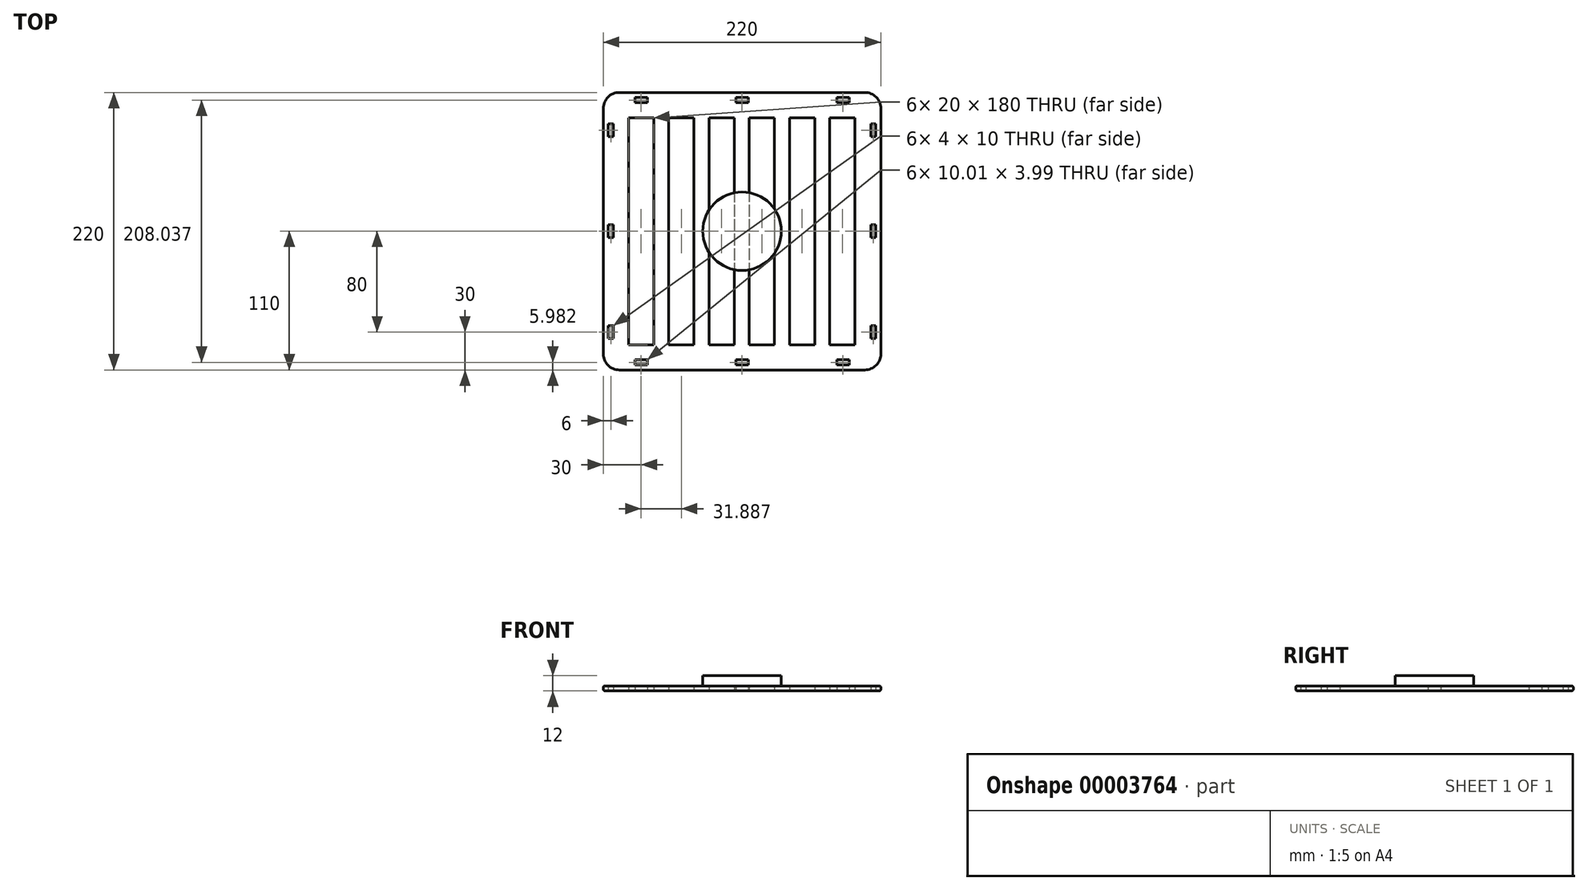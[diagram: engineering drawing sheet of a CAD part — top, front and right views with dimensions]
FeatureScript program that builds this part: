
annotation { "Feature Type Name" : "Feature", "Feature Type Description" : "" }
export const myFeature = defineFeature(function(context is Context, id is Id, definition is map)
    precondition{}
    {
        {
            var Q0;
            Q0=qCreatedBy(makeId("Top.planeOp"),FACE);
            var sketch = newSketch(context, id + "F0", { "sketchPlane" : qUnion([Q0])});
            skLineSegment(sketch, "E0.bottom", {"start": v(-97.3, 110) * mm, "end": v(97.3, 110) * mm});
            skLineSegment(sketch, "E0.top", {"start": v(-97.3, -110) * mm, "end": v(97.3, -110) * mm});
            skLineSegment(sketch, "E0.left", {"start": v(-110, 97.3) * mm, "end": v(-110, -97.3) * mm});
            skLineSegment(sketch, "E0.right", {"start": v(110, 97.3) * mm, "end": v(110, -97.3) * mm});
            skLineSegment(sketch, "E1.bottom", {"start": v(-90, 90) * mm, "end": v(-70, 90) * mm});
            skLineSegment(sketch, "E1.top", {"start": v(-90, -90) * mm, "end": v(-70, -90) * mm});
            skLineSegment(sketch, "E1.left", {"start": v(-90, 90) * mm, "end": v(-90, -90) * mm});
            skLineSegment(sketch, "E1.right", {"start": v(-70, 90) * mm, "end": v(-70, -90) * mm});
            skLineSegment(sketch, "E2.1.0.0", {"start": v(-58.11, 90) * mm, "end": v(-38.11, 90) * mm});
            skLineSegment(sketch, "E2.1.0.1", {"start": v(-38.11, 90) * mm, "end": v(-38.11, -90) * mm});
            skLineSegment(sketch, "E2.1.0.2", {"start": v(-58.11, 90) * mm, "end": v(-58.11, -90) * mm});
            skLineSegment(sketch, "E2.1.0.3", {"start": v(-58.11, -90) * mm, "end": v(-38.11, -90) * mm});
            skLineSegment(sketch, "E2.2.0.0", {"start": v(-26.23, 90) * mm, "end": v(-6.23, 90) * mm});
            skLineSegment(sketch, "E2.2.0.1", {"start": v(-6.23, 90) * mm, "end": v(-6.23, -90) * mm});
            skLineSegment(sketch, "E2.2.0.2", {"start": v(-26.23, 90) * mm, "end": v(-26.23, -90) * mm});
            skLineSegment(sketch, "E2.2.0.3", {"start": v(-26.23, -90) * mm, "end": v(-6.23, -90) * mm});
            skLineSegment(sketch, "E2.3.0.0", {"start": v(5.66, 90) * mm, "end": v(25.66, 90) * mm});
            skLineSegment(sketch, "E2.3.0.1", {"start": v(25.66, 90) * mm, "end": v(25.66, -90) * mm});
            skLineSegment(sketch, "E2.3.0.2", {"start": v(5.66, 90) * mm, "end": v(5.66, -90) * mm});
            skLineSegment(sketch, "E2.3.0.3", {"start": v(5.66, -90) * mm, "end": v(25.66, -90) * mm});
            skLineSegment(sketch, "E2.4.0.0", {"start": v(37.55, 90) * mm, "end": v(57.55, 90) * mm});
            skLineSegment(sketch, "E2.4.0.1", {"start": v(57.55, 90) * mm, "end": v(57.55, -90) * mm});
            skLineSegment(sketch, "E2.4.0.2", {"start": v(37.55, 90) * mm, "end": v(37.55, -90) * mm});
            skLineSegment(sketch, "E2.4.0.3", {"start": v(37.55, -90) * mm, "end": v(57.55, -90) * mm});
            skLineSegment(sketch, "E2.5.0.0", {"start": v(69.44, 90) * mm, "end": v(89.44, 90) * mm});
            skLineSegment(sketch, "E2.5.0.1", {"start": v(89.44, 90) * mm, "end": v(89.44, -90) * mm});
            skLineSegment(sketch, "E2.5.0.2", {"start": v(69.44, 90) * mm, "end": v(69.44, -90) * mm});
            skLineSegment(sketch, "E2.5.0.3", {"start": v(69.44, -90) * mm, "end": v(89.44, -90) * mm});
            skLineSegment(sketch, "E2.direction1", {"start": v(-90, 90) * mm, "end": v(-58.11, 90) * mm, "construction": true});
            skLineSegment(sketch, "E3", {"start": v(0, 0) * mm, "end": v(-110, 0) * mm, "construction": true});
            skLineSegment(sketch, "E4", {"start": v(0, 0) * mm, "end": v(110, 0) * mm, "construction": true});
            skLineSegment(sketch, "E5.rect.bottom", {"start": v(-106, 5) * mm, "end": v(-102, 5) * mm});
            skLineSegment(sketch, "E5.rect.top", {"start": v(-106, -5) * mm, "end": v(-102, -5) * mm});
            skLineSegment(sketch, "E5.rect.left", {"start": v(-106, 5) * mm, "end": v(-106, -5) * mm});
            skLineSegment(sketch, "E5.rect.right", {"start": v(-102, 5) * mm, "end": v(-102, -5) * mm});
            skPoint(sketch, "E5.rect.middle", {"position": v(-104, 0) * mm});
            skLineSegment(sketch, "E6", {"start": v(0, 0) * mm, "end": v(0, 110) * mm, "construction": true});
            skLineSegment(sketch, "E7.0.MirrorCS", {"start": v(106, -5) * mm, "end": v(102, -5) * mm});
            skLineSegment(sketch, "E8.0.MirrorCS", {"start": v(102, 5) * mm, "end": v(102, -5) * mm});
            skLineSegment(sketch, "E9.0.MirrorCS", {"start": v(106, 5) * mm, "end": v(102, 5) * mm});
            skLineSegment(sketch, "E10.0.MirrorCS", {"start": v(106, 5) * mm, "end": v(106, -5) * mm});
            skLineSegment(sketch, "E11.0.1.0", {"start": v(-106, 85) * mm, "end": v(-102, 85) * mm});
            skPoint(sketch, "E11.0.1.1", {"position": v(-104, 80) * mm});
            skLineSegment(sketch, "E11.0.1.2", {"start": v(-102, 85) * mm, "end": v(-102, 75) * mm});
            skLineSegment(sketch, "E11.0.1.3", {"start": v(-106, 75) * mm, "end": v(-102, 75) * mm});
            skLineSegment(sketch, "E11.0.1.4", {"start": v(-106, 85) * mm, "end": v(-106, 75) * mm});
            skLineSegment(sketch, "E11.0.1.5", {"start": v(-58.11, 170) * mm, "end": v(-58.11, -10) * mm});
            skLineSegment(sketch, "E11.direction1", {"start": v(-106, 5) * mm, "end": v(-80.6, 5) * mm, "construction": true});
            skLineSegment(sketch, "E11.direction2", {"start": v(-106, 5) * mm, "end": v(-106, 85) * mm, "construction": true});
            skLineSegment(sketch, "E12.0.1.0", {"start": v(-106, -75) * mm, "end": v(-102, -75) * mm});
            skLineSegment(sketch, "E12.0.1.1", {"start": v(-102, -75) * mm, "end": v(-102, -85) * mm});
            skLineSegment(sketch, "E12.0.1.2", {"start": v(-106, -75) * mm, "end": v(-106, -85) * mm});
            skLineSegment(sketch, "E12.0.1.3", {"start": v(-106, -85) * mm, "end": v(-102, -85) * mm});
            skLineSegment(sketch, "E12.direction2", {"start": v(-106, 5) * mm, "end": v(-106, -75) * mm, "construction": true});
            skLineSegment(sketch, "E13.0.MirrorCS", {"start": v(106, 85) * mm, "end": v(102, 85) * mm});
            skLineSegment(sketch, "E14.0.MirrorCS", {"start": v(106, 85) * mm, "end": v(106, 75) * mm});
            skLineSegment(sketch, "E15.0.MirrorCS", {"start": v(106, 75) * mm, "end": v(102, 75) * mm});
            skLineSegment(sketch, "E16.0.MirrorCS", {"start": v(102, 85) * mm, "end": v(102, 75) * mm});
            skLineSegment(sketch, "E17.0.MirrorCS", {"start": v(106, -75) * mm, "end": v(102, -75) * mm});
            skLineSegment(sketch, "E18.0.MirrorCS", {"start": v(106, -75) * mm, "end": v(106, -85) * mm});
            skLineSegment(sketch, "E19.0.MirrorCS", {"start": v(106, -85) * mm, "end": v(102, -85) * mm});
            skLineSegment(sketch, "E20.0.MirrorCS", {"start": v(102, -75) * mm, "end": v(102, -85) * mm});
            skLineSegment(sketch, "E21.rect.bottom", {"start": v(-5, 102.02) * mm, "end": v(5, 102.02) * mm});
            skLineSegment(sketch, "E21.rect.top", {"start": v(-5, 106.01) * mm, "end": v(5, 106.01) * mm});
            skLineSegment(sketch, "E21.rect.left", {"start": v(-5, 102.02) * mm, "end": v(-5, 106.01) * mm});
            skLineSegment(sketch, "E21.rect.right", {"start": v(5, 102.02) * mm, "end": v(5, 106.01) * mm});
            skPoint(sketch, "E21.rect.middle", {"position": v(0, 104.02) * mm});
            skLineSegment(sketch, "E22.1.0.0", {"start": v(75, 106.01) * mm, "end": v(85, 106.01) * mm});
            skLineSegment(sketch, "E22.1.0.1", {"start": v(75, 102.02) * mm, "end": v(75, 106.01) * mm});
            skLineSegment(sketch, "E22.1.0.2", {"start": v(75, 102.02) * mm, "end": v(85, 102.02) * mm});
            skLineSegment(sketch, "E22.1.0.3", {"start": v(85, 102.02) * mm, "end": v(85, 106.01) * mm});
            skLineSegment(sketch, "E22.direction1", {"start": v(-5, 106.01) * mm, "end": v(75, 106.01) * mm, "construction": true});
            skLineSegment(sketch, "E23.1.0.0", {"start": v(-85, 106.01) * mm, "end": v(-75, 106.01) * mm});
            skLineSegment(sketch, "E23.1.0.1", {"start": v(-85, 102.02) * mm, "end": v(-85, 106.01) * mm});
            skLineSegment(sketch, "E23.1.0.2", {"start": v(-85, 102.02) * mm, "end": v(-75, 102.02) * mm});
            skLineSegment(sketch, "E23.1.0.3", {"start": v(-75, 102.02) * mm, "end": v(-75, 106.01) * mm});
            skLineSegment(sketch, "E23.direction1", {"start": v(-5, 106.01) * mm, "end": v(-85, 106.01) * mm, "construction": true});
            skLineSegment(sketch, "E24.0.MirrorCS", {"start": v(-85, -106.01) * mm, "end": v(-75, -106.01) * mm});
            skLineSegment(sketch, "E25.0.MirrorCS", {"start": v(-85, -102.02) * mm, "end": v(-75, -102.02) * mm});
            skLineSegment(sketch, "E26.0.MirrorCS", {"start": v(-75, -102.02) * mm, "end": v(-75, -106.01) * mm});
            skLineSegment(sketch, "E27.0.MirrorCS", {"start": v(-85, -102.02) * mm, "end": v(-85, -106.01) * mm});
            skLineSegment(sketch, "E28.0.MirrorCS", {"start": v(-5, -106.01) * mm, "end": v(5, -106.01) * mm});
            skLineSegment(sketch, "E29.0.MirrorCS", {"start": v(-5, -102.02) * mm, "end": v(-5, -106.01) * mm});
            skLineSegment(sketch, "E30.0.MirrorCS", {"start": v(-5, -102.02) * mm, "end": v(5, -102.02) * mm});
            skLineSegment(sketch, "E31.0.MirrorCS", {"start": v(5, -102.02) * mm, "end": v(5, -106.01) * mm});
            skLineSegment(sketch, "E32.0.MirrorCS", {"start": v(75, -106.01) * mm, "end": v(85, -106.01) * mm});
            skLineSegment(sketch, "E33.0.MirrorCS", {"start": v(85, -102.02) * mm, "end": v(85, -106.01) * mm});
            skLineSegment(sketch, "E34.0.MirrorCS", {"start": v(75, -102.02) * mm, "end": v(85, -102.02) * mm});
            skLineSegment(sketch, "E35.0.MirrorCS", {"start": v(75, -102.02) * mm, "end": v(75, -106.01) * mm});
            skPoint(sketch, "E36.visualSharp", {"position": v(-110, 110) * mm});
            skArc(sketch, "E36.filletArc", {"start": v(-97.3, 110) * mm, "mid": v(-106.28, 106.28) * mm, "end": v(-110, 97.3) * mm});
            skPoint(sketch, "E37.visualSharp", {"position": v(-110, -110) * mm});
            skArc(sketch, "E37.filletArc", {"start": v(-110, -97.3) * mm, "mid": v(-106.28, -106.28) * mm, "end": v(-97.3, -110) * mm});
            skPoint(sketch, "E38.visualSharp", {"position": v(110, -110) * mm});
            skArc(sketch, "E38.filletArc", {"start": v(97.3, -110) * mm, "mid": v(106.28, -106.28) * mm, "end": v(110, -97.3) * mm});
            skPoint(sketch, "E39.visualSharp", {"position": v(110, 110) * mm});
            skArc(sketch, "E39.filletArc", {"start": v(110, 97.3) * mm, "mid": v(106.28, 106.28) * mm, "end": v(97.3, 110) * mm});
            skSolve(sketch);
        }
        {
            var Q0;
            Q0=makeQuery(id+"F0.imprint","IMPRINT",FACE,{"disambiguationData":[TD([[makeQuery(id+"F0.imprint","IMPRINT",EDGE,{"derivedFrom":sQuery(id+"F0.wireOp",EDGE,"E0.top")}),1.0]])]});
            extrude(context, id + "F1", {"entities" : qUnion([Q0]), "depth" : 4 * mm});
        }
        {
            var Q0;
            Q0=makeQuery(id+"F1.opExtrude","CAP_FACE",FACE,{"disambiguationData":[OSD([sQuery(id+"F0.wireOp",EDGE,"E0.bottom"),sQuery(id+"F0.wireOp",EDGE,"E0.top"),sQuery(id+"F0.wireOp",EDGE,"E0.left"),sQuery(id+"F0.wireOp",EDGE,"E0.right"),sQuery(id+"F0.wireOp",EDGE,"E1.bottom"),sQuery(id+"F0.wireOp",EDGE,"E1.top"),sQuery(id+"F0.wireOp",EDGE,"E1.left"),sQuery(id+"F0.wireOp",EDGE,"E1.right"),sQuery(id+"F0.wireOp",EDGE,"E2.1.0.0"),sQuery(id+"F0.wireOp",EDGE,"E2.1.0.1"),sQuery(id+"F0.wireOp",EDGE,"E2.1.0.2"),sQuery(id+"F0.wireOp",EDGE,"E2.1.0.3"),sQuery(id+"F0.wireOp",EDGE,"E2.2.0.0"),sQuery(id+"F0.wireOp",EDGE,"E2.2.0.1"),sQuery(id+"F0.wireOp",EDGE,"E2.2.0.2"),sQuery(id+"F0.wireOp",EDGE,"E2.2.0.3"),sQuery(id+"F0.wireOp",EDGE,"E2.3.0.0"),sQuery(id+"F0.wireOp",EDGE,"E2.3.0.1"),sQuery(id+"F0.wireOp",EDGE,"E2.3.0.2"),sQuery(id+"F0.wireOp",EDGE,"E2.3.0.3"),sQuery(id+"F0.wireOp",EDGE,"E2.4.0.0"),sQuery(id+"F0.wireOp",EDGE,"E2.4.0.1"),sQuery(id+"F0.wireOp",EDGE,"E2.4.0.2"),sQuery(id+"F0.wireOp",EDGE,"E2.4.0.3"),sQuery(id+"F0.wireOp",EDGE,"E2.5.0.0"),sQuery(id+"F0.wireOp",EDGE,"E2.5.0.1"),sQuery(id+"F0.wireOp",EDGE,"E2.5.0.2"),sQuery(id+"F0.wireOp",EDGE,"E2.5.0.3"),sQuery(id+"F0.wireOp",EDGE,"E5.rect.bottom"),sQuery(id+"F0.wireOp",EDGE,"E5.rect.top"),sQuery(id+"F0.wireOp",EDGE,"E5.rect.left"),sQuery(id+"F0.wireOp",EDGE,"E5.rect.right"),sQuery(id+"F0.wireOp",EDGE,"E7.0.MirrorCS"),sQuery(id+"F0.wireOp",EDGE,"E8.0.MirrorCS"),sQuery(id+"F0.wireOp",EDGE,"E9.0.MirrorCS"),sQuery(id+"F0.wireOp",EDGE,"E10.0.MirrorCS"),sQuery(id+"F0.wireOp",EDGE,"E11.0.1.0"),sQuery(id+"F0.wireOp",EDGE,"E11.0.1.2"),sQuery(id+"F0.wireOp",EDGE,"E11.0.1.3"),sQuery(id+"F0.wireOp",EDGE,"E11.0.1.4"),sQuery(id+"F0.wireOp",EDGE,"E11.0.1.5"),sQuery(id+"F0.wireOp",EDGE,"E12.0.1.0"),sQuery(id+"F0.wireOp",EDGE,"E12.0.1.1"),sQuery(id+"F0.wireOp",EDGE,"E12.0.1.2"),sQuery(id+"F0.wireOp",EDGE,"E12.0.1.3"),sQuery(id+"F0.wireOp",EDGE,"E13.0.MirrorCS"),sQuery(id+"F0.wireOp",EDGE,"E14.0.MirrorCS"),sQuery(id+"F0.wireOp",EDGE,"E15.0.MirrorCS"),sQuery(id+"F0.wireOp",EDGE,"E16.0.MirrorCS"),sQuery(id+"F0.wireOp",EDGE,"E17.0.MirrorCS"),sQuery(id+"F0.wireOp",EDGE,"E18.0.MirrorCS"),sQuery(id+"F0.wireOp",EDGE,"E19.0.MirrorCS"),sQuery(id+"F0.wireOp",EDGE,"E20.0.MirrorCS"),sQuery(id+"F0.wireOp",EDGE,"E21.rect.bottom"),sQuery(id+"F0.wireOp",EDGE,"E21.rect.top"),sQuery(id+"F0.wireOp",EDGE,"E21.rect.left"),sQuery(id+"F0.wireOp",EDGE,"E21.rect.right"),sQuery(id+"F0.wireOp",EDGE,"E22.1.0.0"),sQuery(id+"F0.wireOp",EDGE,"E22.1.0.1"),sQuery(id+"F0.wireOp",EDGE,"E22.1.0.2"),sQuery(id+"F0.wireOp",EDGE,"E22.1.0.3"),sQuery(id+"F0.wireOp",EDGE,"E23.1.0.0"),sQuery(id+"F0.wireOp",EDGE,"E23.1.0.1"),sQuery(id+"F0.wireOp",EDGE,"E23.1.0.2"),sQuery(id+"F0.wireOp",EDGE,"E23.1.0.3"),sQuery(id+"F0.wireOp",EDGE,"E24.0.MirrorCS"),sQuery(id+"F0.wireOp",EDGE,"E25.0.MirrorCS"),sQuery(id+"F0.wireOp",EDGE,"E26.0.MirrorCS"),sQuery(id+"F0.wireOp",EDGE,"E27.0.MirrorCS"),sQuery(id+"F0.wireOp",EDGE,"E28.0.MirrorCS"),sQuery(id+"F0.wireOp",EDGE,"E29.0.MirrorCS"),sQuery(id+"F0.wireOp",EDGE,"E30.0.MirrorCS"),sQuery(id+"F0.wireOp",EDGE,"E31.0.MirrorCS"),sQuery(id+"F0.wireOp",EDGE,"E32.0.MirrorCS"),sQuery(id+"F0.wireOp",EDGE,"E33.0.MirrorCS"),sQuery(id+"F0.wireOp",EDGE,"E34.0.MirrorCS"),sQuery(id+"F0.wireOp",EDGE,"E35.0.MirrorCS"),sQuery(id+"F0.wireOp",EDGE,"E36.filletArc"),sQuery(id+"F0.wireOp",EDGE,"E37.filletArc"),sQuery(id+"F0.wireOp",EDGE,"E38.filletArc"),sQuery(id+"F0.wireOp",EDGE,"E39.filletArc")])],"isStart":false});
            var sketch = newSketch(context, id + "F2", { "sketchPlane" : qUnion([Q0])});
            skCircle(sketch, "E40", {"center": v(0, 0) * mm, "radius": 31.11 * mm});
            skSolve(sketch);
        }
        {
            var Q0;
            {var subQ0=makeQuery(id+"F1.opExtrude","CAP_EDGE",EDGE,{"disambiguationData":[OSD([sQuery(id+"F0.wireOp",EDGE,"E2.3.0.2")])],"isStart":false});var subQ1=sQuery(id+"F2.wireOp",EDGE,"E40");var subQ3=makeQuery(id+"F2.imprint","INTERSECT",VERTEX,{"disambiguationData":[OD(0.0)],"derivedFrom":[subQ0,subQ1]});Q0=makeQuery(id+"F2.imprint","IMPRINT",FACE,{"disambiguationData":[TD([[makeQuery(id+"F2.imprint","IMPRINT",EDGE,{"disambiguationData":[TD([[subQ3,1.0]])],"derivedFrom":subQ1}),1.0]])]});}
            var Q1;
            {var subQ0=makeQuery(id+"F1.opExtrude","CAP_EDGE",EDGE,{"disambiguationData":[OSD([sQuery(id+"F0.wireOp",EDGE,"E2.3.0.1")])],"isStart":false});var subQ1=sQuery(id+"F2.wireOp",EDGE,"E40");var subQ3=makeQuery(id+"F2.imprint","INTERSECT",VERTEX,{"disambiguationData":[OD(0.0)],"derivedFrom":[subQ0,subQ1]});Q1=makeQuery(id+"F2.imprint","IMPRINT",FACE,{"disambiguationData":[TD([[makeQuery(id+"F2.imprint","IMPRINT",EDGE,{"disambiguationData":[TD([[subQ3,1.0]])],"derivedFrom":subQ1}),1.0]])]});}
            var Q2;
            {var subQ0=makeQuery(id+"F1.opExtrude","CAP_EDGE",EDGE,{"disambiguationData":[OSD([sQuery(id+"F0.wireOp",EDGE,"E2.3.0.2")])],"isStart":false});var subQ1=sQuery(id+"F2.wireOp",EDGE,"E40");var subQ3=makeQuery(id+"F2.imprint","INTERSECT",VERTEX,{"disambiguationData":[OD(0.0)],"derivedFrom":[subQ0,subQ1]});Q2=makeQuery(id+"F2.imprint","IMPRINT",FACE,{"disambiguationData":[TD([[makeQuery(id+"F2.imprint","IMPRINT",EDGE,{"disambiguationData":[TD([[subQ3,-1.0]])],"derivedFrom":subQ1}),1.0]])]});}
            var Q3;
            {var subQ0=makeQuery(id+"F1.opExtrude","CAP_EDGE",EDGE,{"disambiguationData":[OSD([sQuery(id+"F0.wireOp",EDGE,"E2.2.0.1")])],"isStart":false});var subQ1=sQuery(id+"F2.wireOp",EDGE,"E40");var subQ3=makeQuery(id+"F2.imprint","INTERSECT",VERTEX,{"disambiguationData":[OD(0.0)],"derivedFrom":[subQ0,subQ1]});Q3=makeQuery(id+"F2.imprint","IMPRINT",FACE,{"disambiguationData":[TD([[makeQuery(id+"F2.imprint","IMPRINT",EDGE,{"disambiguationData":[TD([[subQ3,-1.0]])],"derivedFrom":subQ1}),1.0]])]});}
            var Q4;
            {var subQ0=makeQuery(id+"F1.opExtrude","CAP_EDGE",EDGE,{"disambiguationData":[OSD([sQuery(id+"F0.wireOp",EDGE,"E2.2.0.2")])],"isStart":false});var subQ1=sQuery(id+"F2.wireOp",EDGE,"E40");var subQ3=makeQuery(id+"F2.imprint","INTERSECT",VERTEX,{"disambiguationData":[OD(0.0)],"derivedFrom":[subQ0,subQ1]});Q4=makeQuery(id+"F2.imprint","IMPRINT",FACE,{"disambiguationData":[TD([[makeQuery(id+"F2.imprint","IMPRINT",EDGE,{"disambiguationData":[TD([[subQ3,-1.0]])],"derivedFrom":subQ1}),1.0]])]});}
            extrude(context, id + "F3", {"entities" : qUnion([Q0, Q1, Q2, Q3, Q4]), "depth" : 8 * mm});
        }
        {
            var Q0;
            Q0=makeQuery(id+"F1.opExtrude","CAP_EDGE",EDGE,{"disambiguationData":[OSD([sQuery(id+"F0.wireOp",EDGE,"E0.top")])],"isStart":false});
            var Q1;
            Q1=makeQuery(id+"F1.opExtrude","CAP_EDGE",EDGE,{"disambiguationData":[OSD([sQuery(id+"F0.wireOp",EDGE,"E0.left")])],"isStart":false});
            var Q2;
            Q2=makeQuery(id+"F1.opExtrude","CAP_EDGE",EDGE,{"disambiguationData":[OSD([sQuery(id+"F0.wireOp",EDGE,"E0.bottom")])],"isStart":false});
            var Q3;
            Q3=makeQuery(id+"F1.opExtrude","CAP_EDGE",EDGE,{"disambiguationData":[OSD([sQuery(id+"F0.wireOp",EDGE,"E0.right")])],"isStart":false});
            var Q4;
            Q4=makeQuery(id+"F1.opExtrude","CAP_EDGE",EDGE,{"disambiguationData":[OSD([sQuery(id+"F0.wireOp",EDGE,"E0.right")])],"isStart":true});
            var Q5;
            Q5=makeQuery(id+"F1.opExtrude","CAP_EDGE",EDGE,{"disambiguationData":[OSD([sQuery(id+"F0.wireOp",EDGE,"E0.bottom")])],"isStart":true});
            var Q6;
            {var subQ0=sQuery(id+"F0.wireOp",EDGE,"E0.bottom");var subQ1=sQuery(id+"F0.wireOp",EDGE,"E39.filletArc");var subQ2=sQuery(id+"F0.wireOp",EDGE,"E0.right");Q6=qUnion([makeQuery(id+"F1.opExtrude","SWEPT_EDGE",EDGE,{"disambiguationData":[OSD([subQ0,sQuery(id+"F0.wireOp",EDGE,"E36.filletArc")])]}),makeQuery(id+"F1.opExtrude","SWEPT_EDGE",EDGE,{"disambiguationData":[OSD([subQ0,subQ1])]}),makeQuery(id+"F1.opExtrude","SWEPT_EDGE",EDGE,{"disambiguationData":[OSD([subQ2,subQ1])]}),makeQuery(id+"F1.opExtrude","SWEPT_EDGE",EDGE,{"disambiguationData":[OSD([subQ2,sQuery(id+"F0.wireOp",EDGE,"E38.filletArc")])]})]);}
            var Q7;
            Q7=makeQuery(id+"F1.opExtrude","CAP_EDGE",EDGE,{"disambiguationData":[OSD([sQuery(id+"F0.wireOp",EDGE,"E0.left")])],"isStart":true});
            var Q8;
            Q8=makeQuery(id+"F1.opExtrude","CAP_EDGE",EDGE,{"disambiguationData":[OSD([sQuery(id+"F0.wireOp",EDGE,"E0.top")])],"isStart":true});
            var Q9;
            {var subQ0=sQuery(id+"F0.wireOp",EDGE,"E0.top");var subQ1=sQuery(id+"F0.wireOp",EDGE,"E37.filletArc");var subQ2=sQuery(id+"F0.wireOp",EDGE,"E0.left");Q9=qUnion([makeQuery(id+"F1.opExtrude","SWEPT_EDGE",EDGE,{"disambiguationData":[OSD([subQ0,subQ1])]}),makeQuery(id+"F1.opExtrude","SWEPT_EDGE",EDGE,{"disambiguationData":[OSD([subQ0,sQuery(id+"F0.wireOp",EDGE,"E38.filletArc")])]}),makeQuery(id+"F1.opExtrude","SWEPT_EDGE",EDGE,{"disambiguationData":[OSD([subQ2,sQuery(id+"F0.wireOp",EDGE,"E36.filletArc")])]}),makeQuery(id+"F1.opExtrude","SWEPT_EDGE",EDGE,{"disambiguationData":[OSD([subQ2,subQ1])]})]);}
            var Q10;
            {var subQ0=sQuery(id+"F0.wireOp",EDGE,"E0.bottom");var subQ1=sQuery(id+"F0.wireOp",EDGE,"E36.filletArc");var subQ2=sQuery(id+"F0.wireOp",EDGE,"E0.left");Q10=qUnion([makeQuery(id+"F1.opExtrude","SWEPT_EDGE",EDGE,{"disambiguationData":[OSD([subQ0,subQ1])]}),makeQuery(id+"F1.opExtrude","SWEPT_EDGE",EDGE,{"disambiguationData":[OSD([subQ0,sQuery(id+"F0.wireOp",EDGE,"E39.filletArc")])]}),makeQuery(id+"F1.opExtrude","SWEPT_EDGE",EDGE,{"disambiguationData":[OSD([subQ2,subQ1])]}),makeQuery(id+"F1.opExtrude","SWEPT_EDGE",EDGE,{"disambiguationData":[OSD([subQ2,sQuery(id+"F0.wireOp",EDGE,"E37.filletArc")])]})]);}
            fillet(context, id + "F4", {"entities" : qUnion([Q0, Q1, Q2, Q3, Q4, Q5, Q6, Q7, Q8, Q9, Q10]), "radius" : 1.27 * mm, "tangentPropagation" : true, "allowEdgeOverflow" : false});
        }
    });
